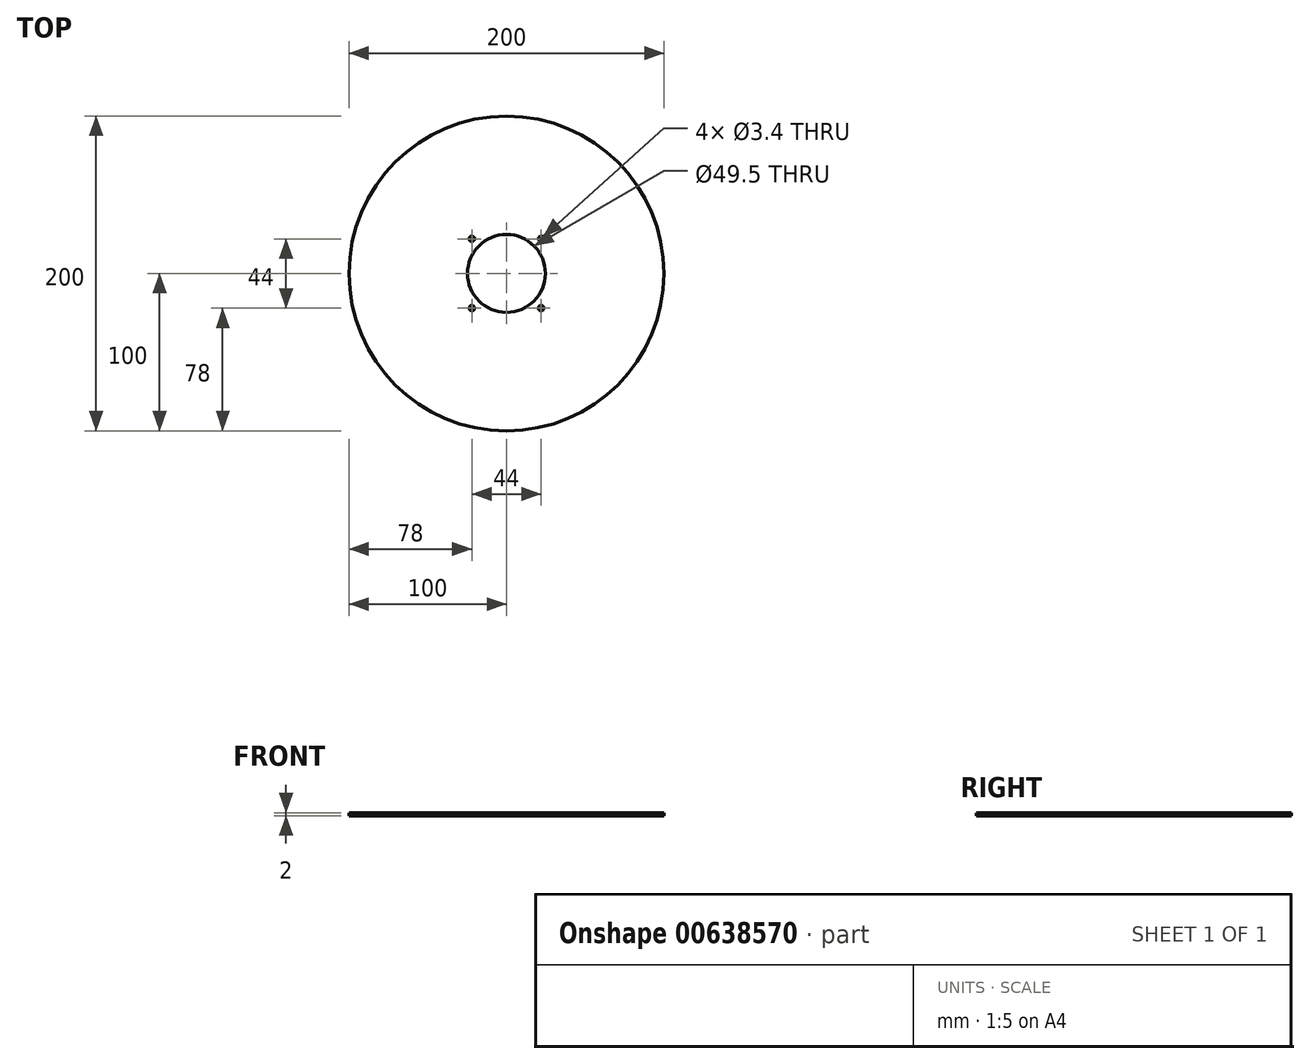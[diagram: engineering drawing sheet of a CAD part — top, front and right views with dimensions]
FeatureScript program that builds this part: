
annotation { "Feature Type Name" : "Feature", "Feature Type Description" : "" }
export const myFeature = defineFeature(function(context is Context, id is Id, definition is map)
    precondition{}
    {
        {
            var Q0;
            Q0=qCreatedBy(makeId("Top.planeOp"),FACE);
            var sketch = newSketch(context, id + "F0", { "sketchPlane" : qUnion([Q0])});
            skCircle(sketch, "E0", {"center": v(0, 0) * mm, "radius": 24.75 * mm});
            skCircle(sketch, "E1", {"center": v(0, 0) * mm, "radius": 100 * mm});
            skLineSegment(sketch, "E2.bottom", {"start": v(-22, -22) * mm, "end": v(22, -22) * mm, "construction": true});
            skLineSegment(sketch, "E2.top", {"start": v(-22, 22) * mm, "end": v(22, 22) * mm, "construction": true});
            skLineSegment(sketch, "E2.left", {"start": v(-22, -22) * mm, "end": v(-22, 22) * mm, "construction": true});
            skLineSegment(sketch, "E2.right", {"start": v(22, -22) * mm, "end": v(22, 22) * mm, "construction": true});
            skCircle(sketch, "E3", {"center": v(-22, -22) * mm, "radius": 1.7 * mm});
            skCircle(sketch, "E4", {"center": v(22, -22) * mm, "radius": 1.7 * mm});
            skCircle(sketch, "E5", {"center": v(22, 22) * mm, "radius": 1.7 * mm});
            skCircle(sketch, "E6", {"center": v(-22, 22) * mm, "radius": 1.7 * mm});
            skSolve(sketch);
        }
        {
            var Q0;
            Q0=qSketchRegion(id+"F0",true);
            extrude(context, id + "F1", {"entities" : qUnion([Q0]), "depth" : 2 * mm, "offsetDistance" : 25 * mm});
        }
    });
